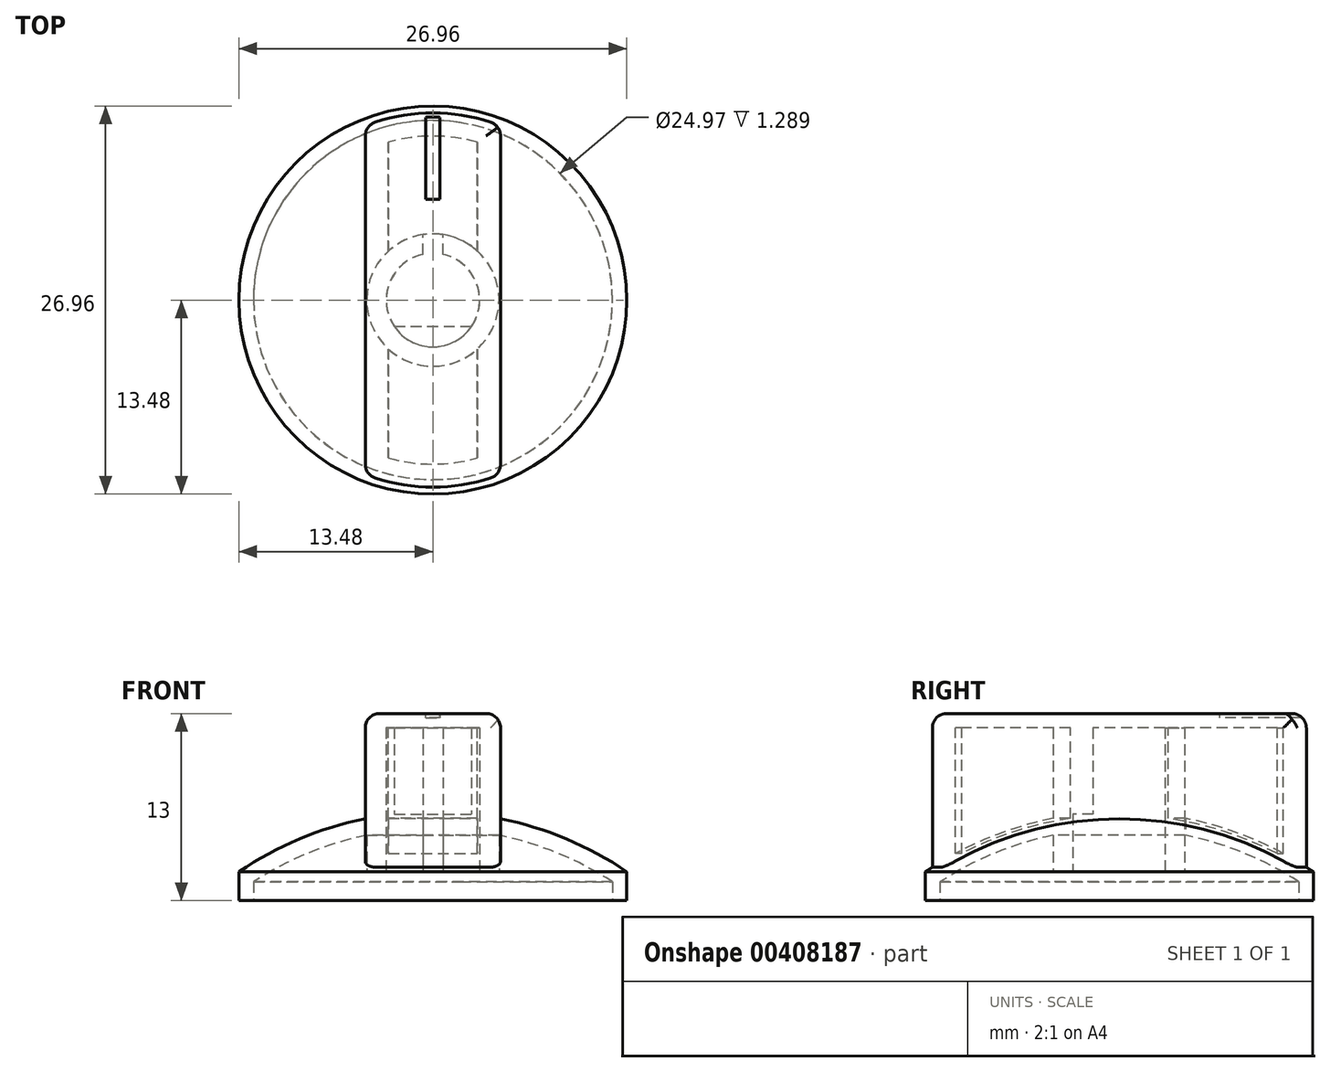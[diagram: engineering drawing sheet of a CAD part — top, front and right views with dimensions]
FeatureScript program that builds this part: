
annotation { "Feature Type Name" : "Feature", "Feature Type Description" : "" }
export const myFeature = defineFeature(function(context is Context, id is Id, definition is map)
    precondition{}
    {
        {
            var Q0;
            Q0=qCreatedBy(makeId("Top.planeOp"),FACE);
            var sketch = newSketch(context, id + "F0", { "sketchPlane" : qUnion([Q0])});
            skArc(sketch, "E0", {"start": v(-0.7, 3.17) * mm, "mid": v(0, -3.25) * mm, "end": v(0.7, 3.17) * mm});
            skArc(sketch, "E1", {"start": v(-0.7, 4.55) * mm, "mid": v(0, -4.6) * mm, "end": v(0.7, 4.55) * mm});
            skLineSegment(sketch, "E2", {"start": v(-0.7, 3.17) * mm, "end": v(-0.7, 4.55) * mm});
            skLineSegment(sketch, "E3", {"start": v(0.7, 3.17) * mm, "end": v(0.7, 4.55) * mm});
            skPoint(sketch, "E4.orphan", {"position": v(-0.7, 0) * mm});
            skPoint(sketch, "E5.orphan", {"position": v(0.7, 0) * mm});
            skSolve(sketch);
        }
        {
            var Q0;
            Q0 = qSketchRegion(id + "F0", true);
            extrude(context, id + "F1", {"entities" : qUnion([Q0]), "depth" : 10 * mm});
        }
        {
            var Q0;
            Q0=qCreatedBy(makeId("Top.planeOp"),FACE);
            cPlane(context, id + "F2", {"entities" : qUnion([Q0]), "cplaneType" : CPlaneType.OFFSET, "offset" : 4 * mm, "width" : 150 * mm, "height" : 150 * mm});
        }
        {
            var Q0;
            Q0=qCreatedBy(id+"F2.planeOp",FACE);
            var sketch = newSketch(context, id + "F3", { "sketchPlane" : qUnion([Q0])});
            skLineSegment(sketch, "E6", {"start": v(-2.69, -1.83) * mm, "end": v(2.69, -1.83) * mm});
            skArc(sketch, "E7", {"start": v(-2.69, -1.83) * mm, "mid": v(0, -3.25) * mm, "end": v(2.69, -1.83) * mm});
            skSolve(sketch);
        }
        {
            var Q0;
            Q0 = qSketchRegion(id + "F3", true);
            extrude(context, id + "F4", {"entities" : qUnion([Q0]), "operationType" : NewBodyOperationType.ADD, "depth" : 6 * mm});
        }
        {
            var Q0;
            Q0=qCreatedBy(makeId("Right.planeOp"),FACE);
            var sketch = newSketch(context, id + "F5", { "sketchPlane" : qUnion([Q0])});
            skArc(sketch, "E8", {"start": v(13.48, 0) * mm, "mid": v(9.23, 2.3) * mm, "end": v(4.6, 3.7) * mm});
            skLineSegment(sketch, "E9", {"start": v(12.48, -2) * mm, "end": v(13.48, -2) * mm});
            skLineSegment(sketch, "E10", {"start": v(13.48, -2) * mm, "end": v(13.48, 0) * mm});
            skLineSegment(sketch, "E11", {"start": v(12.48, -2) * mm, "end": v(12.48, -0.71) * mm});
            skArc(sketch, "E12", {"start": v(12.48, -0.71) * mm, "mid": v(8.7, 1.28) * mm, "end": v(4.6, 2.53) * mm});
            skLineSegment(sketch, "E13", {"start": v(4.6, 0) * mm, "end": v(4.6, 3.7) * mm});
            skSolve(sketch);
        }
        {
            var Q0;
            Q0=qCreatedBy(makeId("Right.planeOp"),FACE);
            var sketch = newSketch(context, id + "F6", { "sketchPlane" : qUnion([Q0])});
            skLineSegment(sketch, "E14", {"start": v(0, 0) * mm, "end": v(0, 13.28) * mm});
            skSolve(sketch);
        }
        {
            var Q0;
            Q0 = qSketchRegion(id + "F5", true);
            var Q1;
            Q1=sQuery(id+"F6.wireOp",EDGE,"E14");
            revolve(context, id + "F7", {"operationType" : NewBodyOperationType.ADD, "entities" : qUnion([Q0]), "axis" : qUnion([Q1]), "revolveType" : RevolveType.FULL});
        }
        {
            var Q0;
            Q0=qCreatedBy(makeId("Top.planeOp"),FACE);
            cPlane(context, id + "F8", {"entities" : qUnion([Q0]), "cplaneType" : CPlaneType.OFFSET, "offset" : 10 * mm, "width" : 150 * mm, "height" : 150 * mm});
        }
        {
            var Q0;
            Q0=qCreatedBy(id+"F8.planeOp",FACE);
            var sketch = newSketch(context, id + "F9", { "sketchPlane" : qUnion([Q0])});
            skLineSegment(sketch, "E15", {"start": v(-4.7, 12.12) * mm, "end": v(-4.7, -12.12) * mm});
            skLineSegment(sketch, "E16", {"start": v(4.7, 12.12) * mm, "end": v(4.7, -12.12) * mm});
            skArc(sketch, "E17", {"start": v(-4.7, -12.12) * mm, "mid": v(0, -13) * mm, "end": v(4.7, -12.12) * mm});
            skArc(sketch, "E18.trimOffspring", {"start": v(4.7, 12.12) * mm, "mid": v(0, 13) * mm, "end": v(-4.7, 12.12) * mm});
            skArc(sketch, "E19", {"start": v(-3.1, -10.97) * mm, "mid": v(0, -11.4) * mm, "end": v(3.1, -10.97) * mm});
            skLineSegment(sketch, "E20", {"start": v(-3.1, 10.97) * mm, "end": v(-3.1, 3.4) * mm});
            skLineSegment(sketch, "E21", {"start": v(3.1, 10.97) * mm, "end": v(3.1, 3.4) * mm});
            skArc(sketch, "E22.trimOffspring", {"start": v(3.1, 10.97) * mm, "mid": v(0, 11.4) * mm, "end": v(-3.1, 10.97) * mm});
            skArc(sketch, "E23", {"start": v(-3.1, 3.4) * mm, "mid": v(-4.6, 0) * mm, "end": v(-3.1, -3.4) * mm});
            skLineSegment(sketch, "E24.trimOffspring", {"start": v(3.1, -3.4) * mm, "end": v(3.1, -10.97) * mm});
            skLineSegment(sketch, "E25.trimOffspring", {"start": v(-3.1, -3.4) * mm, "end": v(-3.1, -10.97) * mm});
            skArc(sketch, "E26.trimOffspring", {"start": v(3.1, -3.4) * mm, "mid": v(4.6, 0) * mm, "end": v(3.1, 3.4) * mm});
            skSolve(sketch);
        }
        {
            var Q0;
            Q0 = qSketchRegion(id + "F9", true);
            var Q1;
            Q1=makeQuery(id+"F7.opRevolve","SWEPT_FACE",FACE,{"disambiguationData":[OSD([sQuery(id+"F5.wireOp",EDGE,"E8")])]});
            extrude(context, id + "F10", {"entities" : qUnion([Q0]), "operationType" : NewBodyOperationType.ADD, "endBound" : BoundingType.UP_TO_SURFACE, "oppositeDirection" : true, "endBoundEntityFace" : qUnion([Q1]), "depth" : 25 * mm});
        }
        {
            var Q0;
            Q0=makeQuery(id+"F10.boolean.opBoolean","MERGE",FACE,{"derivedFrom":[makeQuery(id+"F4.boolean.opBoolean","MERGE",FACE,{"derivedFrom":[makeQuery(id+"F1.opExtrude","CAP_FACE",FACE,{"disambiguationData":[OSD([sQuery(id+"F0.wireOp",EDGE,"E0"),sQuery(id+"F0.wireOp",EDGE,"E1"),sQuery(id+"F0.wireOp",EDGE,"E2"),sQuery(id+"F0.wireOp",EDGE,"E3")])],"isStart":false}),makeQuery(id+"F4.opExtrude","CAP_FACE",FACE,{"disambiguationData":[OSD([sQuery(id+"F3.wireOp",EDGE,"E6"),sQuery(id+"F3.wireOp",EDGE,"E7")])],"isStart":false})]}),makeQuery(id+"F10.opExtrude","CAP_FACE",FACE,{"disambiguationData":[OSD([sQuery(id+"F9.wireOp",EDGE,"E15"),sQuery(id+"F9.wireOp",EDGE,"E16"),sQuery(id+"F9.wireOp",EDGE,"E17"),sQuery(id+"F9.wireOp",EDGE,"E18.trimOffspring"),sQuery(id+"F9.wireOp",EDGE,"E19"),sQuery(id+"F9.wireOp",EDGE,"E20"),sQuery(id+"F9.wireOp",EDGE,"E21"),sQuery(id+"F9.wireOp",EDGE,"E22.trimOffspring"),sQuery(id+"F9.wireOp",EDGE,"E23"),sQuery(id+"F9.wireOp",EDGE,"E24.trimOffspring"),sQuery(id+"F9.wireOp",EDGE,"E25.trimOffspring"),sQuery(id+"F9.wireOp",EDGE,"E26.trimOffspring")])],"isStart":true})]});
            var sketch = newSketch(context, id + "F11", { "sketchPlane" : qUnion([Q0])});
            skLineSegment(sketch, "E27", {"start": v(4.7, -12.12) * mm, "end": v(4.7, 12.12) * mm});
            skLineSegment(sketch, "E28", {"start": v(-4.7, -12.12) * mm, "end": v(-4.7, 12.12) * mm});
            skArc(sketch, "E29", {"start": v(-4.7, -12.12) * mm, "mid": v(0, -13) * mm, "end": v(4.7, -12.12) * mm});
            skArc(sketch, "E30.trimOffspring", {"start": v(4.7, 12.12) * mm, "mid": v(0, 13) * mm, "end": v(-4.7, 12.12) * mm});
            skSolve(sketch);
        }
        {
            var Q0;
            Q0 = qSketchRegion(id + "F11", true);
            extrude(context, id + "F12", {"entities" : qUnion([Q0]), "operationType" : NewBodyOperationType.ADD, "depth" : 1 * mm});
        }
        {
            var Q0;
            Q0=makeQuery(id+"F12.opExtrude","CAP_FACE",FACE,{"disambiguationData":[OSD([sQuery(id+"F11.wireOp",EDGE,"E27"),sQuery(id+"F11.wireOp",EDGE,"E28"),sQuery(id+"F11.wireOp",EDGE,"E29"),sQuery(id+"F11.wireOp",EDGE,"E30.trimOffspring")])],"isStart":false});
            var sketch = newSketch(context, id + "F13", { "sketchPlane" : qUnion([Q0])});
            skLineSegment(sketch, "E31", {"start": v(-0.5, 13) * mm, "end": v(-0.5, 7) * mm});
            skPoint(sketch, "E32.end.orphan", {"position": v(0, 13) * mm});
            skPoint(sketch, "E33.end.orphan", {"position": v(0, 7.03) * mm});
            skLineSegment(sketch, "E34", {"start": v(-0.5, 7) * mm, "end": v(0.5, 7) * mm});
            skLineSegment(sketch, "E35", {"start": v(0.5, 7) * mm, "end": v(0.5, 13) * mm});
            skArc(sketch, "E36", {"start": v(0.5, 13) * mm, "mid": v(0, 13) * mm, "end": v(-0.5, 13) * mm});
            skSolve(sketch);
        }
        {
            var Q0;
            Q0 = qSketchRegion(id + "F13", true);
            extrude(context, id + "F14", {"entities" : qUnion([Q0]), "operationType" : NewBodyOperationType.REMOVE, "oppositeDirection" : true, "depth" : 0.3 * mm});
        }
        {
            var Q0;
            Q0=makeQuery(id+"F12.boolean.opBoolean","MERGE",EDGE,{"derivedFrom":[makeQuery(id+"F10.opExtrude","SWEPT_EDGE",EDGE,{"disambiguationData":[OSD([sQuery(id+"F9.wireOp",EDGE,"E16"),sQuery(id+"F9.wireOp",EDGE,"E18.trimOffspring")])]}),makeQuery(id+"F12.opExtrude","SWEPT_EDGE",EDGE,{"disambiguationData":[OSD([sQuery(id+"F11.wireOp",EDGE,"E27"),sQuery(id+"F11.wireOp",EDGE,"E30.trimOffspring")])]})]});
            var Q1;
            Q1=makeQuery(id+"F12.boolean.opBoolean","MERGE",EDGE,{"derivedFrom":[makeQuery(id+"F10.opExtrude","SWEPT_EDGE",EDGE,{"disambiguationData":[OSD([sQuery(id+"F9.wireOp",EDGE,"E15"),sQuery(id+"F9.wireOp",EDGE,"E18.trimOffspring")])]}),makeQuery(id+"F12.opExtrude","SWEPT_EDGE",EDGE,{"disambiguationData":[OSD([sQuery(id+"F11.wireOp",EDGE,"E28"),sQuery(id+"F11.wireOp",EDGE,"E30.trimOffspring")])]})]});
            var Q2;
            Q2=makeQuery(id+"F12.boolean.opBoolean","MERGE",EDGE,{"derivedFrom":[makeQuery(id+"F10.opExtrude","SWEPT_EDGE",EDGE,{"disambiguationData":[OSD([sQuery(id+"F9.wireOp",EDGE,"E16"),sQuery(id+"F9.wireOp",EDGE,"E17")])]}),makeQuery(id+"F12.opExtrude","SWEPT_EDGE",EDGE,{"disambiguationData":[OSD([sQuery(id+"F11.wireOp",EDGE,"E27"),sQuery(id+"F11.wireOp",EDGE,"E29")])]})]});
            var Q3;
            Q3=makeQuery(id+"F12.boolean.opBoolean","MERGE",EDGE,{"derivedFrom":[makeQuery(id+"F10.opExtrude","SWEPT_EDGE",EDGE,{"disambiguationData":[OSD([sQuery(id+"F9.wireOp",EDGE,"E15"),sQuery(id+"F9.wireOp",EDGE,"E17")])]}),makeQuery(id+"F12.opExtrude","SWEPT_EDGE",EDGE,{"disambiguationData":[OSD([sQuery(id+"F11.wireOp",EDGE,"E28"),sQuery(id+"F11.wireOp",EDGE,"E29")])]})]});
            var Q4;
            Q4=makeQuery(id+"F12.opExtrude","CAP_EDGE",EDGE,{"disambiguationData":[OSD([sQuery(id+"F11.wireOp",EDGE,"E27")])],"isStart":false});
            var Q5;
            Q5=makeQuery(id+"F12.opExtrude","CAP_EDGE",EDGE,{"disambiguationData":[OSD([sQuery(id+"F11.wireOp",EDGE,"E29")])],"isStart":false});
            var Q6;
            {var subQ1=sQuery(id+"F11.wireOp",EDGE,"E30.trimOffspring");Q6=makeQuery(id+"F14.boolean.opBoolean","SPLIT",EDGE,{"disambiguationData":[TD([makeQuery(id+"F10.opExtrude","SWEPT_FACE",FACE,{"disambiguationData":[OSD([sQuery(id+"F9.wireOp",EDGE,"E15")])]})])],"derivedFrom":makeQuery(id+"F12.opExtrude","CAP_EDGE",EDGE,{"disambiguationData":[OSD([subQ1])],"isStart":false})});}
            var Q7;
            Q7=makeQuery(id+"F12.opExtrude","CAP_EDGE",EDGE,{"disambiguationData":[OSD([sQuery(id+"F11.wireOp",EDGE,"E28")])],"isStart":false});
            fillet(context, id + "F15", {"entities" : qUnion([Q0, Q1, Q2, Q3, Q4, Q5, Q6, Q7]), "radius" : 1 * mm, "tangentPropagation" : true, "allowEdgeOverflow" : false});
        }
    });
